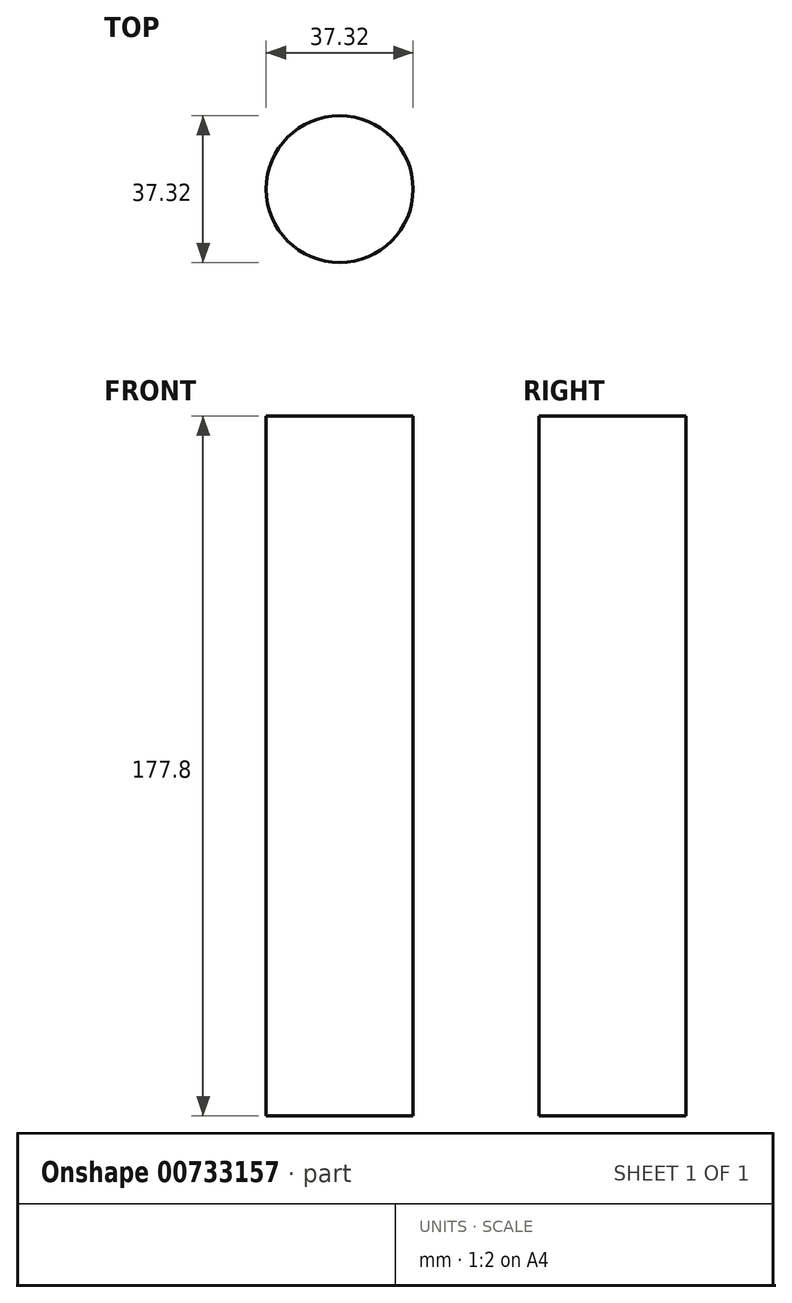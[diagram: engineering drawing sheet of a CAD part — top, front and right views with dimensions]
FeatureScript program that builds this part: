
annotation { "Feature Type Name" : "Feature", "Feature Type Description" : "" }
export const myFeature = defineFeature(function(context is Context, id is Id, definition is map)
    precondition{}
    {
        {
            var Q0;
            Q0=qCreatedBy(makeId("Top.planeOp"),FACE);
            var sketch = newSketch(context, id + "F0", { "sketchPlane" : qUnion([Q0])});
            skCircle(sketch, "E0", {"center": v(0, 0) * mm, "radius": 18.66 * mm});
            skSolve(sketch);
        }
        {
            var Q0;
            Q0=makeQuery(id+"F0.imprint","IMPRINT",FACE,{"disambiguationData":[TD([[makeQuery(id+"F0.imprint","IMPRINT",EDGE,{"derivedFrom":sQuery(id+"F0.wireOp",EDGE,"E0")}),1.0]])]});
            extrude(context, id + "F1", {"entities" : qUnion([Q0]), "depth" : 177.8 * mm, "offsetDistance" : 25.4 * mm});
        }
    });
